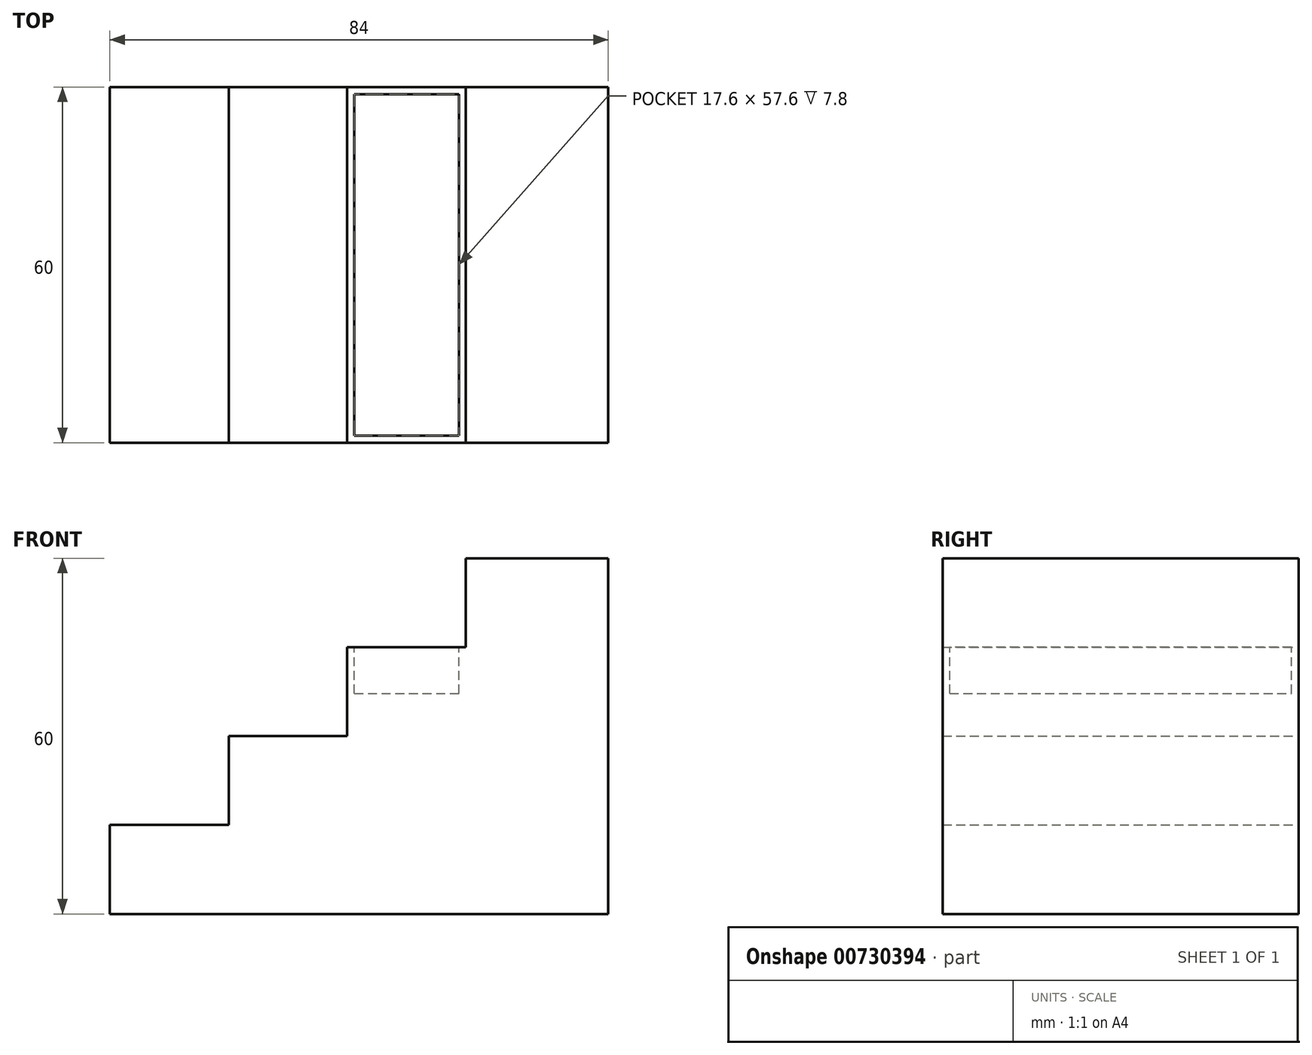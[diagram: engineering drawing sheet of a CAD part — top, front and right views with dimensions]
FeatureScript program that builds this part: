
annotation { "Feature Type Name" : "Feature", "Feature Type Description" : "" }
export const myFeature = defineFeature(function(context is Context, id is Id, definition is map)
    precondition{}
    {
        {
            var Q0;
            Q0=qCreatedBy(makeId("Front.planeOp"),FACE);
            var sketch = newSketch(context, id + "F0", { "sketchPlane" : qUnion([Q0])});
            skLineSegment(sketch, "E0", {"start": v(0, 0) * mm, "end": v(-84, 0) * mm});
            skLineSegment(sketch, "E1", {"start": v(-84, 0) * mm, "end": v(-84, 15) * mm});
            skLineSegment(sketch, "E2", {"start": v(-84, 15) * mm, "end": v(-64, 15) * mm});
            skLineSegment(sketch, "E3", {"start": v(-64, 15) * mm, "end": v(-64, 30) * mm});
            skLineSegment(sketch, "E4", {"start": v(-64, 30) * mm, "end": v(-44, 30) * mm});
            skLineSegment(sketch, "E5", {"start": v(-44, 30) * mm, "end": v(-44, 45) * mm});
            skLineSegment(sketch, "E6", {"start": v(-44, 45) * mm, "end": v(-24, 45) * mm});
            skLineSegment(sketch, "E7", {"start": v(-24, 45) * mm, "end": v(-24, 60) * mm});
            skLineSegment(sketch, "E8", {"start": v(-24, 60) * mm, "end": v(0, 60) * mm});
            skLineSegment(sketch, "E9", {"start": v(0, 60) * mm, "end": v(0, 0) * mm});
            skSolve(sketch);
        }
        {
            var Q0;
            Q0=makeQuery(id+"F0.imprint","IMPRINT",FACE,{"disambiguationData":[TD([[makeQuery(id+"F0.imprint","IMPRINT",EDGE,{"derivedFrom":sQuery(id+"F0.wireOp",EDGE,"E0")}),-1.0]])]});
            extrude(context, id + "F1", {"entities" : qUnion([Q0]), "depth" : 60 * mm, "offsetDistance" : 25 * mm});
        }
        {
            var Q0;
            Q0=makeQuery(id+"F1.opExtrude","SWEPT_FACE",FACE,{"disambiguationData":[OSD([sQuery(id+"F0.wireOp",EDGE,"E6")])]});
            var sketch = newSketch(context, id + "F2", { "sketchPlane" : qUnion([Q0])});
            skLineSegment(sketch, "E10.bottom", {"start": v(-25.2, -1.2) * mm, "end": v(-42.8, -1.2) * mm});
            skLineSegment(sketch, "E10.top", {"start": v(-25.2, -58.8) * mm, "end": v(-42.8, -58.8) * mm});
            skLineSegment(sketch, "E10.left", {"start": v(-25.2, -1.2) * mm, "end": v(-25.2, -58.8) * mm});
            skLineSegment(sketch, "E10.right", {"start": v(-42.8, -1.2) * mm, "end": v(-42.8, -58.8) * mm});
            skSolve(sketch);
        }
        {
            var Q0;
            Q0=makeQuery(id+"F2.imprint","IMPRINT",FACE,{"disambiguationData":[TD([[makeQuery(id+"F2.imprint","IMPRINT",EDGE,{"derivedFrom":sQuery(id+"F2.wireOp",EDGE,"E10.bottom")}),1.0]])]});
            extrude(context, id + "F3", {"entities" : qUnion([Q0]), "operationType" : NewBodyOperationType.REMOVE, "oppositeDirection" : true, "depth" : 25 * mm, "offsetDistance" : 25 * mm});
        }
        {
            var Q0;
            Q0=makeQuery(id+"F3.boolean.opBoolean","COPY",FACE,{"derivedFrom":makeQuery(id+"F3.opExtrude","CAP_FACE",FACE,{"disambiguationData":[OSD([sQuery(id+"F2.wireOp",EDGE,"E10.bottom"),sQuery(id+"F2.wireOp",EDGE,"E10.top"),sQuery(id+"F2.wireOp",EDGE,"E10.left"),sQuery(id+"F2.wireOp",EDGE,"E10.right")])],"isStart":false})});
            extrude(context, id + "F4", {"entities" : qUnion([Q0]), "depth" : 16 * mm, "offsetDistance" : 25 * mm});
        }
        {
            var Q0;
            Q0=makeQuery(id+"F4.opExtrude","CAP_FACE",FACE,{"disambiguationData":[OSD([sQuery(id+"F2.wireOp",EDGE,"E10.bottom"),sQuery(id+"F2.wireOp",EDGE,"E10.top"),sQuery(id+"F2.wireOp",EDGE,"E10.left"),sQuery(id+"F2.wireOp",EDGE,"E10.right")])],"isStart":false});
            var sketch = newSketch(context, id + "F5", { "sketchPlane" : qUnion([Q0])});
            skLineSegment(sketch, "E11.0", {"start": v(-44, -60) * mm, "end": v(-24, -60) * mm});
            skLineSegment(sketch, "E11.1", {"start": v(-44, 0) * mm, "end": v(-44, -60) * mm});
            skLineSegment(sketch, "E11.2", {"start": v(-24, 0) * mm, "end": v(-44, 0) * mm});
            skLineSegment(sketch, "E11.3", {"start": v(-24, -60) * mm, "end": v(-24, 0) * mm});
            skSolve(sketch);
        }
        {
            var Q0;
            Q0=makeQuery(id+"F5.imprint","IMPRINT",FACE,{"disambiguationData":[TD([[makeQuery(id+"F5.imprint","IMPRINT",EDGE,{"derivedFrom":sQuery(id+"F5.wireOp",EDGE,"E11.0")}),1.0]])]});
            var Q1;
            Q1=makeQuery(id+"F5.imprint","IMPRINT",FACE,{"disambiguationData":[TD([[makeQuery(id+"F5.imprint","IMPRINT",EDGE,{"derivedFrom":makeQuery(id+"F4.opExtrude","CAP_EDGE",EDGE,{"disambiguationData":[OSD([sQuery(id+"F2.wireOp",EDGE,"E10.bottom")])],"isStart":false})}),1.0]])]});
            extrude(context, id + "F6", {"entities" : qUnion([Q0, Q1]), "operationType" : NewBodyOperationType.ADD, "depth" : 1.2 * mm, "offsetDistance" : 25 * mm});
        }
    });
